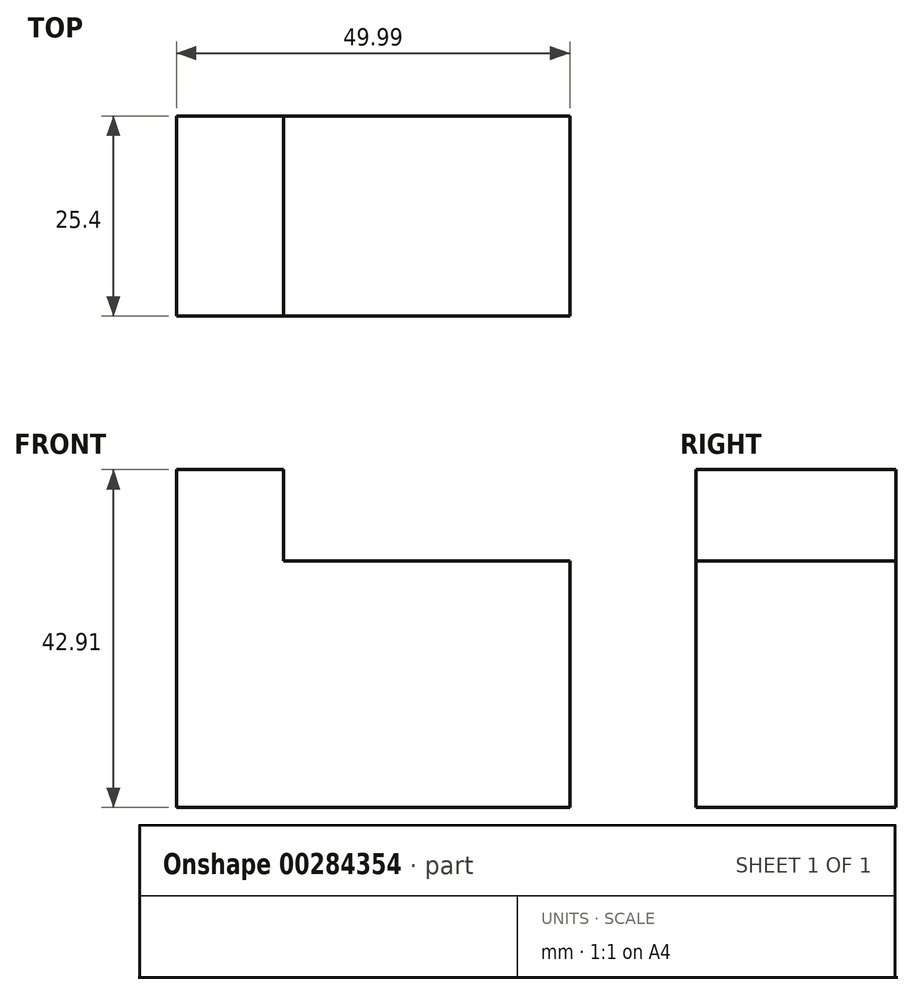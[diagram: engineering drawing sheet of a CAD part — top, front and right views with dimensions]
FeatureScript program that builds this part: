
annotation { "Feature Type Name" : "Feature", "Feature Type Description" : "" }
export const myFeature = defineFeature(function(context is Context, id is Id, definition is map)
    precondition{}
    {
        {
            var Q0;
            Q0=qCreatedBy(makeId("Front.planeOp"),FACE);
            var sketch = newSketch(context, id + "F0", { "sketchPlane" : qUnion([Q0])});
            skLineSegment(sketch, "E0.bottom", {"start": v(0, 31.3) * mm, "end": v(-36.4, 31.3) * mm});
            skLineSegment(sketch, "E0.top", {"start": v(0, 12.04) * mm, "end": v(-36.4, 12.04) * mm});
            skLineSegment(sketch, "E0.left", {"start": v(0, 31.3) * mm, "end": v(0, 12.04) * mm});
            skLineSegment(sketch, "E0.right", {"start": v(-36.4, 31.3) * mm, "end": v(-36.4, 12.04) * mm});
            skLineSegment(sketch, "E1", {"start": v(0, 12.04) * mm, "end": v(0, 0) * mm});
            skLineSegment(sketch, "E2", {"start": v(0, 0) * mm, "end": v(-49.99, 0) * mm});
            skLineSegment(sketch, "E3", {"start": v(-49.99, 0) * mm, "end": v(-49.99, 42.9) * mm});
            skLineSegment(sketch, "E4", {"start": v(-49.99, 42.9) * mm, "end": v(-36.4, 42.9) * mm});
            skLineSegment(sketch, "E5", {"start": v(-36.4, 42.9) * mm, "end": v(-36.4, 31.3) * mm});
            skSolve(sketch);
        }
        {
            var Q0;
            Q0=makeQuery(id+"F0.imprint","IMPRINT",FACE,{"disambiguationData":[TD([[makeQuery(id+"F0.imprint","IMPRINT",EDGE,{"derivedFrom":sQuery(id+"F0.wireOp",EDGE,"E0.top")}),1.0]])]});
            var Q1;
            Q1=makeQuery(id+"F0.imprint","IMPRINT",FACE,{"disambiguationData":[TD([[makeQuery(id+"F0.imprint","IMPRINT",EDGE,{"derivedFrom":sQuery(id+"F0.wireOp",EDGE,"E0.bottom")}),1.0]])]});
            extrude(context, id + "F1", {"entities" : qUnion([Q0, Q1]), "depth" : 25.4 * mm});
        }
    });
